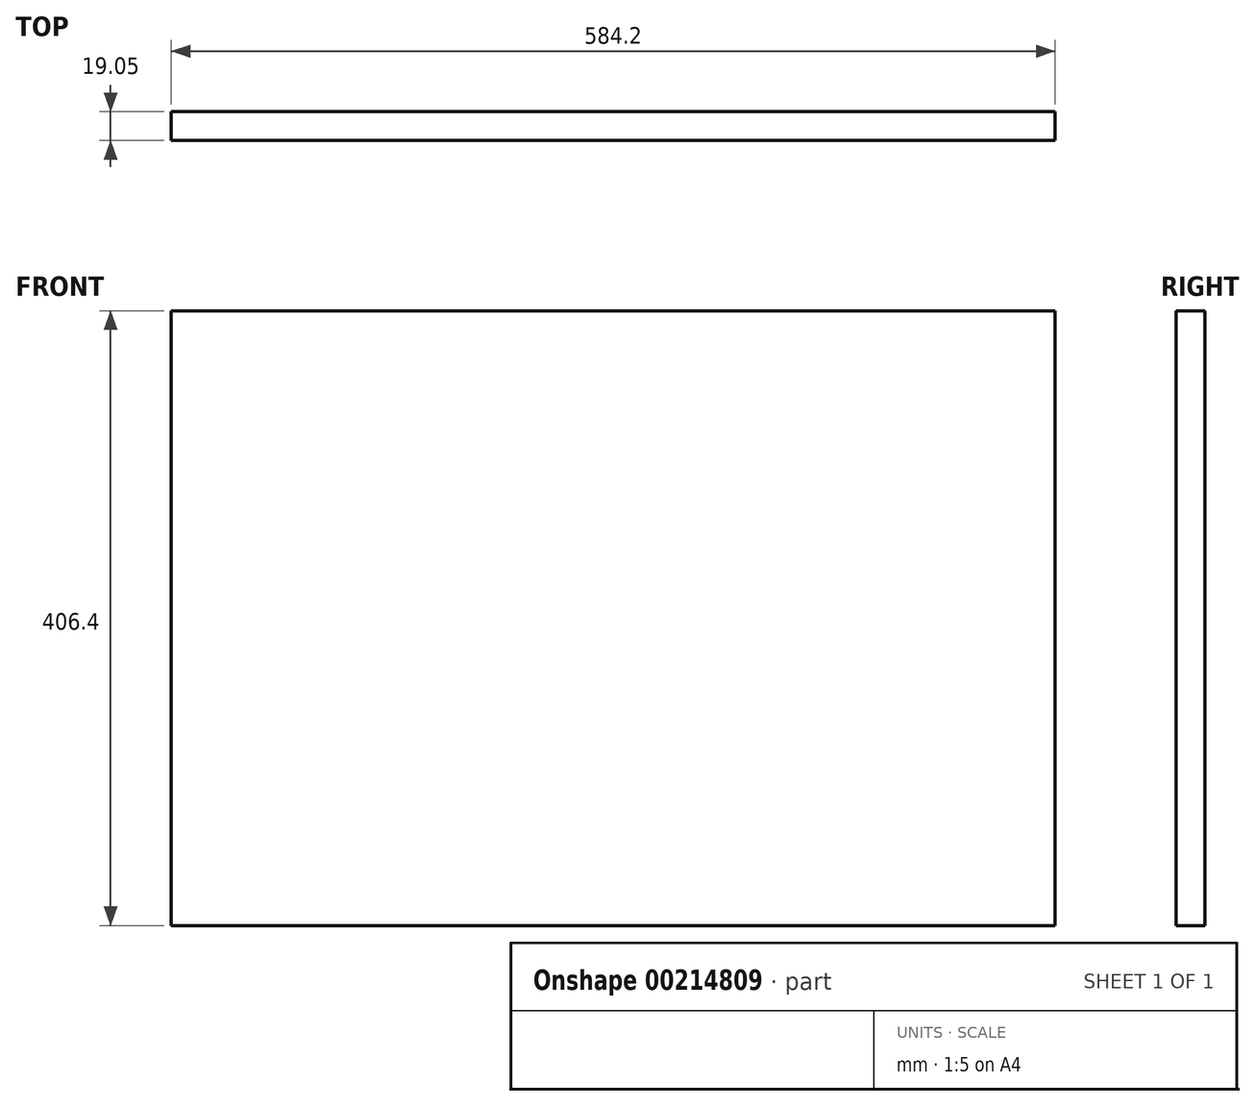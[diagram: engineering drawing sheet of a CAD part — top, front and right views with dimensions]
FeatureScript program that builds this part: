
annotation { "Feature Type Name" : "Feature", "Feature Type Description" : "" }
export const myFeature = defineFeature(function(context is Context, id is Id, definition is map)
    precondition{}
    {
        {
            var Q0;
            Q0=qCreatedBy(makeId("Front.planeOp"),FACE);
            var sketch = newSketch(context, id + "F0", { "sketchPlane" : qUnion([Q0])});
            skLineSegment(sketch, "E0.bottom", {"start": v(0, 0) * mm, "end": v(584.2, 0) * mm});
            skLineSegment(sketch, "E0.top", {"start": v(0, -406.4) * mm, "end": v(584.2, -406.4) * mm});
            skLineSegment(sketch, "E0.left", {"start": v(0, 0) * mm, "end": v(0, -406.4) * mm});
            skLineSegment(sketch, "E0.right", {"start": v(584.2, 0) * mm, "end": v(584.2, -406.4) * mm});
            skSolve(sketch);
        }
        {
            var Q0;
            Q0=makeQuery(id+"F0.imprint","IMPRINT",FACE,{"disambiguationData":[TD([[makeQuery(id+"F0.imprint","IMPRINT",EDGE,{"derivedFrom":sQuery(id+"F0.wireOp",EDGE,"E0.bottom")}),-1.0]])]});
            extrude(context, id + "F1", {"entities" : qUnion([Q0]), "depth" : 19.05 * mm});
        }
    });
